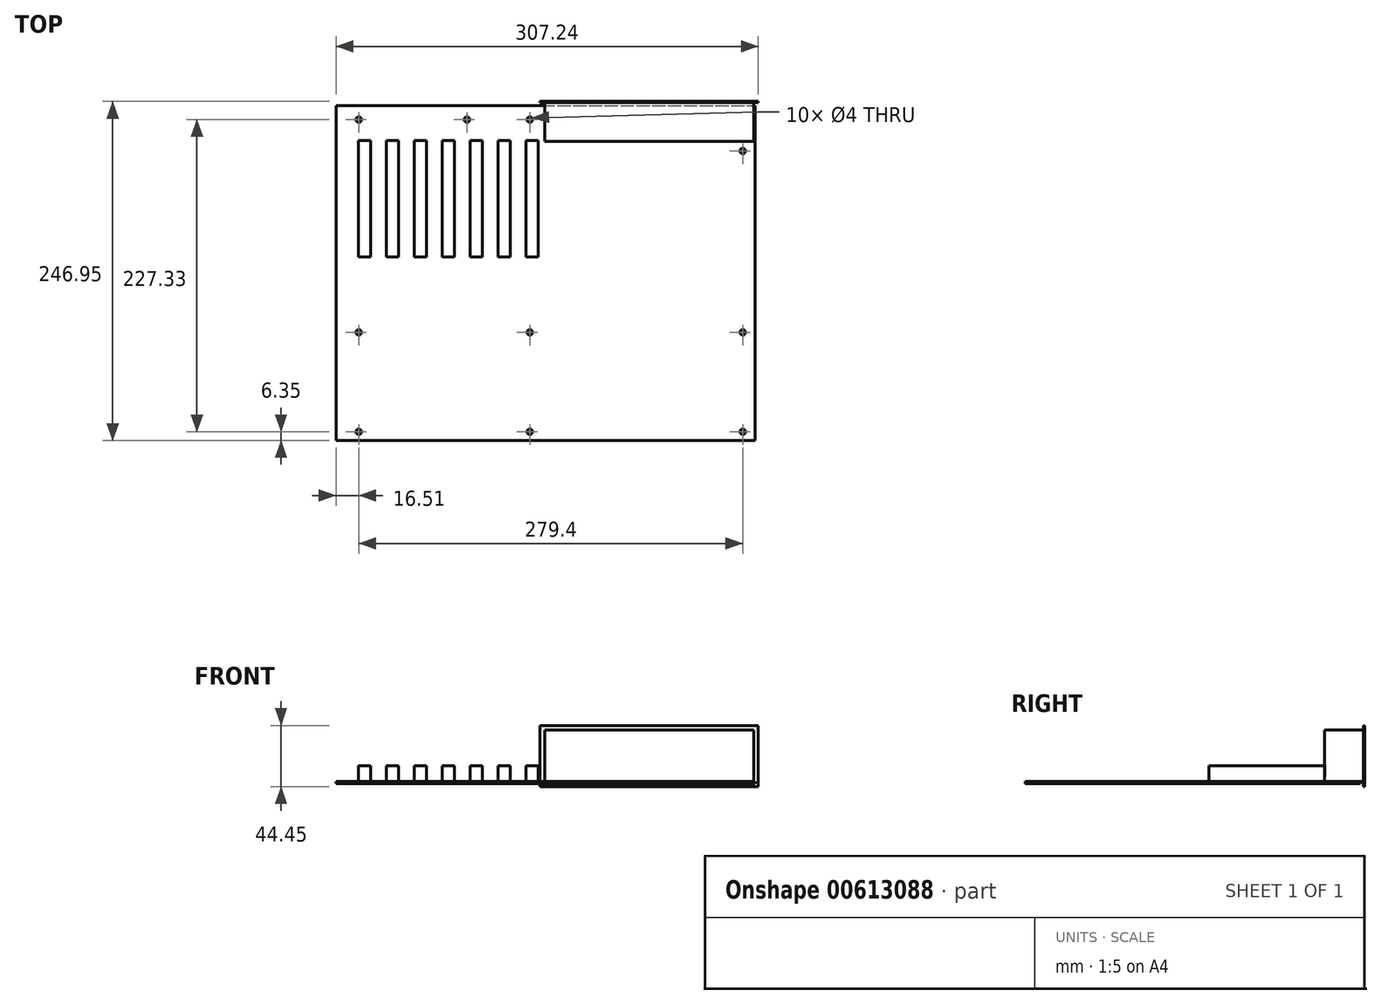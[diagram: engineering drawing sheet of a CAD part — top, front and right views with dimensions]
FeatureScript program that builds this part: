
annotation { "Feature Type Name" : "Feature", "Feature Type Description" : "" }
export const myFeature = defineFeature(function(context is Context, id is Id, definition is map)
    precondition{}
    {
        {
            var Q0;
            Q0=qCreatedBy(makeId("Top.planeOp"),FACE);
            var sketch = newSketch(context, id + "F0", { "sketchPlane" : qUnion([Q0])});
            skLineSegment(sketch, "E0.bottom", {"start": v(0, 0) * mm, "end": v(304.8, 0) * mm});
            skLineSegment(sketch, "E0.top", {"start": v(0, 243.84) * mm, "end": v(304.8, 243.84) * mm});
            skLineSegment(sketch, "E0.left", {"start": v(0, 0) * mm, "end": v(0, 243.84) * mm});
            skLineSegment(sketch, "E0.right", {"start": v(304.8, 0) * mm, "end": v(304.8, 243.84) * mm});
            skLineSegment(sketch, "E1", {"start": v(0, 233.68) * mm, "end": v(304.8, 233.68) * mm, "construction": true});
            skLineSegment(sketch, "E2", {"start": v(295.9, 243.84) * mm, "end": v(295.9, 0) * mm, "construction": true});
            skLineSegment(sketch, "E3", {"start": v(140.97, 243.84) * mm, "end": v(140.97, 0) * mm, "construction": true});
            skLineSegment(sketch, "E4", {"start": v(16.5, 243.84) * mm, "end": v(16.51, 0) * mm, "construction": true});
            skLineSegment(sketch, "E5", {"start": v(0, 6.35) * mm, "end": v(304.8, 6.35) * mm, "construction": true});
            skLineSegment(sketch, "E6", {"start": v(0, 78.74) * mm, "end": v(304.8, 78.74) * mm, "construction": true});
            skCircle(sketch, "E7", {"center": v(16.5, 233.68) * mm, "radius": 2 * mm});
            skCircle(sketch, "E8", {"center": v(16.5, 78.74) * mm, "radius": 2 * mm});
            skCircle(sketch, "E9", {"center": v(16.51, 6.35) * mm, "radius": 2 * mm});
            skCircle(sketch, "E10", {"center": v(140.97, 233.68) * mm, "radius": 2 * mm});
            skCircle(sketch, "E11", {"center": v(140.97, 78.74) * mm, "radius": 2 * mm});
            skCircle(sketch, "E12", {"center": v(140.97, 6.35) * mm, "radius": 2 * mm});
            skCircle(sketch, "E13", {"center": v(295.9, 6.35) * mm, "radius": 2 * mm});
            skCircle(sketch, "E14", {"center": v(295.9, 78.74) * mm, "radius": 2 * mm});
            skCircle(sketch, "E15", {"center": v(295.91, 210.82) * mm, "radius": 2 * mm});
            skCircle(sketch, "E16", {"center": v(95.25, 233.68) * mm, "radius": 2 * mm});
            skSolve(sketch);
        }
        {
            var Q0;
            Q0 = qSketchRegion(id + "F0", true);
            extrude(context, id + "F1", {"entities" : qUnion([Q0]), "depth" : 1.6 * mm, "offsetDistance" : 25 * mm});
        }
        {
            var Q0;
            Q0=makeQuery(id+"F1.opExtrude","CAP_FACE",FACE,{"disambiguationData":[OSD([sQuery(id+"F0.wireOp",EDGE,"E0.bottom"),sQuery(id+"F0.wireOp",EDGE,"E0.top"),sQuery(id+"F0.wireOp",EDGE,"E0.left"),sQuery(id+"F0.wireOp",EDGE,"E0.right"),sQuery(id+"F0.wireOp",EDGE,"E7"),sQuery(id+"F0.wireOp",EDGE,"E8"),sQuery(id+"F0.wireOp",EDGE,"E9"),sQuery(id+"F0.wireOp",EDGE,"E10"),sQuery(id+"F0.wireOp",EDGE,"E11"),sQuery(id+"F0.wireOp",EDGE,"E12"),sQuery(id+"F0.wireOp",EDGE,"E13"),sQuery(id+"F0.wireOp",EDGE,"E14"),sQuery(id+"F0.wireOp",EDGE,"E15"),sQuery(id+"F0.wireOp",EDGE,"E16")])],"isStart":false});
            var sketch = newSketch(context, id + "F2", { "sketchPlane" : qUnion([Q0])});
            skLineSegment(sketch, "E17.bottom", {"start": v(117.78, 218.44) * mm, "end": v(126.67, 218.44) * mm});
            skLineSegment(sketch, "E17.top", {"start": v(117.78, 133.6) * mm, "end": v(126.67, 133.6) * mm});
            skLineSegment(sketch, "E17.left", {"start": v(117.78, 218.44) * mm, "end": v(117.78, 133.6) * mm});
            skLineSegment(sketch, "E17.right", {"start": v(126.67, 218.44) * mm, "end": v(126.67, 133.6) * mm});
            skLineSegment(sketch, "E18", {"start": v(122.22, 218.44) * mm, "end": v(122.22, 133.6) * mm, "construction": true});
            skLineSegment(sketch, "E19.bottom", {"start": v(138.1, 218.44) * mm, "end": v(146.99, 218.44) * mm});
            skLineSegment(sketch, "E19.top", {"start": v(138.1, 133.6) * mm, "end": v(146.99, 133.6) * mm});
            skLineSegment(sketch, "E19.left", {"start": v(138.1, 218.44) * mm, "end": v(138.1, 133.6) * mm});
            skLineSegment(sketch, "E19.right", {"start": v(146.99, 218.44) * mm, "end": v(146.99, 133.6) * mm});
            skLineSegment(sketch, "E20", {"start": v(142.54, 218.44) * mm, "end": v(142.54, 133.6) * mm, "construction": true});
            skLineSegment(sketch, "E21.bottom", {"start": v(77.14, 218.44) * mm, "end": v(86.03, 218.44) * mm});
            skLineSegment(sketch, "E21.top", {"start": v(77.14, 133.6) * mm, "end": v(86.03, 133.6) * mm});
            skLineSegment(sketch, "E21.left", {"start": v(77.14, 218.44) * mm, "end": v(77.14, 133.6) * mm});
            skLineSegment(sketch, "E21.right", {"start": v(86.03, 218.44) * mm, "end": v(86.03, 133.6) * mm});
            skLineSegment(sketch, "E22", {"start": v(81.58, 218.44) * mm, "end": v(81.58, 133.6) * mm, "construction": true});
            skLineSegment(sketch, "E23.bottom", {"start": v(97.46, 218.44) * mm, "end": v(106.35, 218.44) * mm});
            skLineSegment(sketch, "E23.top", {"start": v(97.46, 133.6) * mm, "end": v(106.35, 133.6) * mm});
            skLineSegment(sketch, "E23.left", {"start": v(97.46, 218.44) * mm, "end": v(97.46, 133.6) * mm});
            skLineSegment(sketch, "E23.right", {"start": v(106.35, 218.44) * mm, "end": v(106.35, 133.6) * mm});
            skLineSegment(sketch, "E24", {"start": v(101.9, 218.44) * mm, "end": v(101.9, 133.6) * mm, "construction": true});
            skLineSegment(sketch, "E25.bottom", {"start": v(36.5, 218.44) * mm, "end": v(45.39, 218.44) * mm});
            skLineSegment(sketch, "E25.top", {"start": v(36.5, 133.6) * mm, "end": v(45.39, 133.6) * mm});
            skLineSegment(sketch, "E25.left", {"start": v(36.5, 218.44) * mm, "end": v(36.5, 133.6) * mm});
            skLineSegment(sketch, "E25.right", {"start": v(45.39, 218.44) * mm, "end": v(45.39, 133.6) * mm});
            skLineSegment(sketch, "E26", {"start": v(40.94, 218.44) * mm, "end": v(40.94, 133.6) * mm, "construction": true});
            skLineSegment(sketch, "E27.bottom", {"start": v(56.82, 218.44) * mm, "end": v(65.7, 218.44) * mm});
            skLineSegment(sketch, "E27.top", {"start": v(56.82, 133.6) * mm, "end": v(65.7, 133.6) * mm});
            skLineSegment(sketch, "E27.left", {"start": v(56.82, 218.44) * mm, "end": v(56.82, 133.6) * mm});
            skLineSegment(sketch, "E27.right", {"start": v(65.7, 218.44) * mm, "end": v(65.7, 133.6) * mm});
            skLineSegment(sketch, "E28", {"start": v(61.26, 218.44) * mm, "end": v(61.26, 133.6) * mm, "construction": true});
            skLineSegment(sketch, "E29.bottom", {"start": v(16.18, 218.44) * mm, "end": v(25.07, 218.44) * mm});
            skLineSegment(sketch, "E29.top", {"start": v(16.18, 133.6) * mm, "end": v(25.07, 133.6) * mm});
            skLineSegment(sketch, "E29.left", {"start": v(16.18, 218.44) * mm, "end": v(16.18, 133.6) * mm});
            skLineSegment(sketch, "E29.right", {"start": v(25.07, 218.44) * mm, "end": v(25.07, 133.6) * mm});
            skLineSegment(sketch, "E30", {"start": v(20.62, 218.44) * mm, "end": v(20.62, 133.6) * mm, "construction": true});
            skSolve(sketch);
        }
        {
            var Q0;
            Q0 = qSketchRegion(id + "F2", true);
            extrude(context, id + "F3", {"entities" : qUnion([Q0]), "operationType" : NewBodyOperationType.ADD, "depth" : 11.25 * mm, "offsetDistance" : 25 * mm});
        }
        {
            var Q0;
            Q0=makeQuery(id+"F1.opExtrude","CAP_FACE",FACE,{"disambiguationData":[OSD([sQuery(id+"F0.wireOp",EDGE,"E0.bottom"),sQuery(id+"F0.wireOp",EDGE,"E0.top"),sQuery(id+"F0.wireOp",EDGE,"E0.left"),sQuery(id+"F0.wireOp",EDGE,"E0.right"),sQuery(id+"F0.wireOp",EDGE,"E7"),sQuery(id+"F0.wireOp",EDGE,"E8"),sQuery(id+"F0.wireOp",EDGE,"E9"),sQuery(id+"F0.wireOp",EDGE,"E10"),sQuery(id+"F0.wireOp",EDGE,"E11"),sQuery(id+"F0.wireOp",EDGE,"E12"),sQuery(id+"F0.wireOp",EDGE,"E13"),sQuery(id+"F0.wireOp",EDGE,"E14"),sQuery(id+"F0.wireOp",EDGE,"E15"),sQuery(id+"F0.wireOp",EDGE,"E16")])],"isStart":false});
            var sketch = newSketch(context, id + "F4", { "sketchPlane" : qUnion([Q0])});
            skLineSegment(sketch, "E31.bottom", {"start": v(151.8, 245.95) * mm, "end": v(303.94, 245.95) * mm});
            skLineSegment(sketch, "E31.top", {"start": v(151.8, 217.95) * mm, "end": v(303.94, 217.95) * mm});
            skLineSegment(sketch, "E31.left", {"start": v(151.8, 245.95) * mm, "end": v(151.8, 217.95) * mm});
            skLineSegment(sketch, "E31.right", {"start": v(303.94, 245.95) * mm, "end": v(303.94, 217.95) * mm});
            skSolve(sketch);
        }
        {
            var Q0;
            Q0 = qSketchRegion(id + "F4", true);
            extrude(context, id + "F5", {"entities" : qUnion([Q0]), "operationType" : NewBodyOperationType.ADD, "depth" : 37.34 * mm, "offsetDistance" : 25 * mm});
        }
        {
            var Q0;
            Q0=makeQuery(id+"F5.opExtrude","SWEPT_FACE",FACE,{"disambiguationData":[OSD([sQuery(id+"F4.wireOp",EDGE,"E31.bottom")])]});
            var sketch = newSketch(context, id + "F6", { "sketchPlane" : qUnion([Q0])});
            skLineSegment(sketch, "E32.bottom", {"start": v(-307.24, 42.24) * mm, "end": v(-148.49, 42.24) * mm});
            skLineSegment(sketch, "E32.top", {"start": v(-307.24, -2.2) * mm, "end": v(-148.49, -2.2) * mm});
            skLineSegment(sketch, "E32.left", {"start": v(-307.24, 42.24) * mm, "end": v(-307.24, -2.2) * mm});
            skLineSegment(sketch, "E32.right", {"start": v(-148.49, 42.24) * mm, "end": v(-148.49, -2.2) * mm});
            skSolve(sketch);
        }
        {
            var Q0;
            Q0 = qSketchRegion(id + "F6", true);
            extrude(context, id + "F7", {"entities" : qUnion([Q0]), "operationType" : NewBodyOperationType.ADD, "depth" : 1 * mm, "offsetDistance" : 25 * mm});
        }
    });
